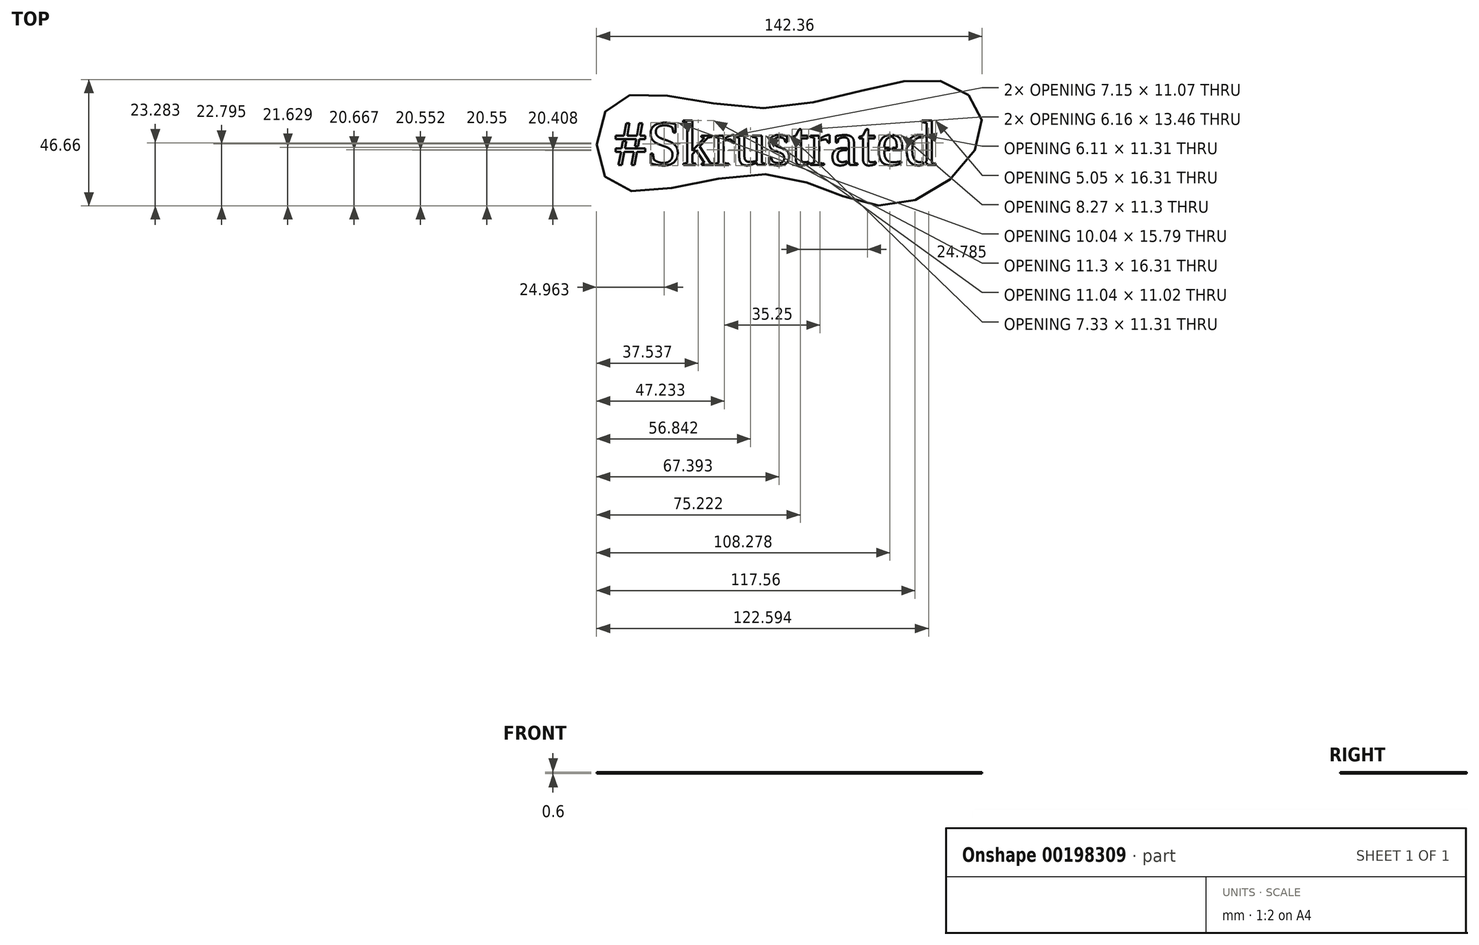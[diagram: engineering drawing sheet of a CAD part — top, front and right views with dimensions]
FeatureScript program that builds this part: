
annotation { "Feature Type Name" : "Feature", "Feature Type Description" : "" }
export const myFeature = defineFeature(function(context is Context, id is Id, definition is map)
    precondition{}
    {
        {
            var Q0;
            Q0=qCreatedBy(makeId("Top.planeOp"),FACE);
            var sketch = newSketch(context, id + "F0", { "sketchPlane" : qUnion([Q0])});
            skText(sketch, "E0", { "text": "#Skrustrated", "fontName": "Tinos-Regular.ttf"});
            skFitSpline(sketch, "E1", {"points": [v(-5.04, 14.15) * mm, v(60, 24.2) * mm, v(75.58, 5.55) * mm, v(43.18, -21.81) * mm, v(-3.93, -10.36) * mm, v(-61.05, -13.8) * mm, v(-60.94, 15.75) * mm, v(-5.04, 14.15) * mm]});
            const initialGuessF0  = {"E0": [-0.06, -0.00685, 1, 0, 0.01692]};
            skSetInitialGuess(sketch, initialGuessF0);
            skSolve(sketch);
        }
        {
            var Q0;
            Q0 = qSketchRegion(id + "F0", true);
            var Q1;
            Q1=makeQuery(id+"F0.imprint","IMPRINT",FACE,{"disambiguationData":[TD([[makeQuery(id+"F0.imprint","IMPRINT",EDGE,{"derivedFrom":sQuery(id+"F0.wireOp",EDGE,"E0.sketch_text.stroke-28")}),1.0]])]});
            var Q2;
            Q2=makeQuery(id+"F0.imprint","IMPRINT",FACE,{"disambiguationData":[TD([[makeQuery(id+"F0.imprint","IMPRINT",EDGE,{"derivedFrom":sQuery(id+"F0.wireOp",EDGE,"E0.sketch_text.stroke-220")}),1.0]])]});
            var Q3;
            Q3=makeQuery(id+"F0.imprint","IMPRINT",FACE,{"disambiguationData":[TD([[makeQuery(id+"F0.imprint","IMPRINT",EDGE,{"derivedFrom":sQuery(id+"F0.wireOp",EDGE,"E0.sketch_text.stroke-262")}),1.0]])]});
            var Q4;
            Q4=makeQuery(id+"F0.imprint","IMPRINT",FACE,{"disambiguationData":[TD([[makeQuery(id+"F0.imprint","IMPRINT",EDGE,{"derivedFrom":sQuery(id+"F0.wireOp",EDGE,"E0.sketch_text.stroke-282")}),1.0]])]});
            extrude(context, id + "F1", {"entities" : qUnion([Q0, Q1, Q2, Q3, Q4]), "depth" : 0.6 * mm});
        }
        {
            var Q0;
            Q0=makeQuery(id+"F1.opExtrude","CAP_FACE",FACE,{"disambiguationData":[OSD([sQuery(id+"F0.wireOp",EDGE,"E0.sketch_text.stroke-0"),sQuery(id+"F0.wireOp",EDGE,"E0.sketch_text.stroke-1"),sQuery(id+"F0.wireOp",EDGE,"E0.sketch_text.stroke-2"),sQuery(id+"F0.wireOp",EDGE,"E0.sketch_text.stroke-3"),sQuery(id+"F0.wireOp",EDGE,"E0.sketch_text.stroke-4"),sQuery(id+"F0.wireOp",EDGE,"E0.sketch_text.stroke-5"),sQuery(id+"F0.wireOp",EDGE,"E0.sketch_text.stroke-6"),sQuery(id+"F0.wireOp",EDGE,"E0.sketch_text.stroke-7"),sQuery(id+"F0.wireOp",EDGE,"E0.sketch_text.stroke-8"),sQuery(id+"F0.wireOp",EDGE,"E0.sketch_text.stroke-9"),sQuery(id+"F0.wireOp",EDGE,"E0.sketch_text.stroke-10"),sQuery(id+"F0.wireOp",EDGE,"E0.sketch_text.stroke-11"),sQuery(id+"F0.wireOp",EDGE,"E0.sketch_text.stroke-12"),sQuery(id+"F0.wireOp",EDGE,"E0.sketch_text.stroke-13"),sQuery(id+"F0.wireOp",EDGE,"E0.sketch_text.stroke-14"),sQuery(id+"F0.wireOp",EDGE,"E0.sketch_text.stroke-15"),sQuery(id+"F0.wireOp",EDGE,"E0.sketch_text.stroke-16"),sQuery(id+"F0.wireOp",EDGE,"E0.sketch_text.stroke-17"),sQuery(id+"F0.wireOp",EDGE,"E0.sketch_text.stroke-18"),sQuery(id+"F0.wireOp",EDGE,"E0.sketch_text.stroke-19"),sQuery(id+"F0.wireOp",EDGE,"E0.sketch_text.stroke-20"),sQuery(id+"F0.wireOp",EDGE,"E0.sketch_text.stroke-21"),sQuery(id+"F0.wireOp",EDGE,"E0.sketch_text.stroke-22"),sQuery(id+"F0.wireOp",EDGE,"E0.sketch_text.stroke-23"),sQuery(id+"F0.wireOp",EDGE,"E0.sketch_text.stroke-24"),sQuery(id+"F0.wireOp",EDGE,"E0.sketch_text.stroke-25"),sQuery(id+"F0.wireOp",EDGE,"E0.sketch_text.stroke-26"),sQuery(id+"F0.wireOp",EDGE,"E0.sketch_text.stroke-27"),sQuery(id+"F0.wireOp",EDGE,"E0.sketch_text.stroke-32"),sQuery(id+"F0.wireOp",EDGE,"E0.sketch_text.stroke-33"),sQuery(id+"F0.wireOp",EDGE,"E0.sketch_text.stroke-34"),sQuery(id+"F0.wireOp",EDGE,"E0.sketch_text.stroke-35"),sQuery(id+"F0.wireOp",EDGE,"E0.sketch_text.stroke-36"),sQuery(id+"F0.wireOp",EDGE,"E0.sketch_text.stroke-37"),sQuery(id+"F0.wireOp",EDGE,"E0.sketch_text.stroke-38"),sQuery(id+"F0.wireOp",EDGE,"E0.sketch_text.stroke-39"),sQuery(id+"F0.wireOp",EDGE,"E0.sketch_text.stroke-40"),sQuery(id+"F0.wireOp",EDGE,"E0.sketch_text.stroke-41"),sQuery(id+"F0.wireOp",EDGE,"E0.sketch_text.stroke-42"),sQuery(id+"F0.wireOp",EDGE,"E0.sketch_text.stroke-43"),sQuery(id+"F0.wireOp",EDGE,"E0.sketch_text.stroke-44"),sQuery(id+"F0.wireOp",EDGE,"E0.sketch_text.stroke-45"),sQuery(id+"F0.wireOp",EDGE,"E0.sketch_text.stroke-46"),sQuery(id+"F0.wireOp",EDGE,"E0.sketch_text.stroke-47"),sQuery(id+"F0.wireOp",EDGE,"E0.sketch_text.stroke-48"),sQuery(id+"F0.wireOp",EDGE,"E0.sketch_text.stroke-49"),sQuery(id+"F0.wireOp",EDGE,"E0.sketch_text.stroke-50"),sQuery(id+"F0.wireOp",EDGE,"E0.sketch_text.stroke-51"),sQuery(id+"F0.wireOp",EDGE,"E0.sketch_text.stroke-52"),sQuery(id+"F0.wireOp",EDGE,"E0.sketch_text.stroke-53"),sQuery(id+"F0.wireOp",EDGE,"E0.sketch_text.stroke-54"),sQuery(id+"F0.wireOp",EDGE,"E0.sketch_text.stroke-55"),sQuery(id+"F0.wireOp",EDGE,"E0.sketch_text.stroke-56"),sQuery(id+"F0.wireOp",EDGE,"E0.sketch_text.stroke-57"),sQuery(id+"F0.wireOp",EDGE,"E0.sketch_text.stroke-58"),sQuery(id+"F0.wireOp",EDGE,"E0.sketch_text.stroke-59"),sQuery(id+"F0.wireOp",EDGE,"E0.sketch_text.stroke-60"),sQuery(id+"F0.wireOp",EDGE,"E0.sketch_text.stroke-61"),sQuery(id+"F0.wireOp",EDGE,"E0.sketch_text.stroke-62"),sQuery(id+"F0.wireOp",EDGE,"E0.sketch_text.stroke-63"),sQuery(id+"F0.wireOp",EDGE,"E0.sketch_text.stroke-64"),sQuery(id+"F0.wireOp",EDGE,"E0.sketch_text.stroke-65"),sQuery(id+"F0.wireOp",EDGE,"E0.sketch_text.stroke-66"),sQuery(id+"F0.wireOp",EDGE,"E0.sketch_text.stroke-67"),sQuery(id+"F0.wireOp",EDGE,"E0.sketch_text.stroke-68"),sQuery(id+"F0.wireOp",EDGE,"E0.sketch_text.stroke-69"),sQuery(id+"F0.wireOp",EDGE,"E0.sketch_text.stroke-70"),sQuery(id+"F0.wireOp",EDGE,"E0.sketch_text.stroke-71"),sQuery(id+"F0.wireOp",EDGE,"E0.sketch_text.stroke-72"),sQuery(id+"F0.wireOp",EDGE,"E0.sketch_text.stroke-73"),sQuery(id+"F0.wireOp",EDGE,"E0.sketch_text.stroke-74"),sQuery(id+"F0.wireOp",EDGE,"E0.sketch_text.stroke-75"),sQuery(id+"F0.wireOp",EDGE,"E0.sketch_text.stroke-76"),sQuery(id+"F0.wireOp",EDGE,"E0.sketch_text.stroke-77"),sQuery(id+"F0.wireOp",EDGE,"E0.sketch_text.stroke-78"),sQuery(id+"F0.wireOp",EDGE,"E0.sketch_text.stroke-79"),sQuery(id+"F0.wireOp",EDGE,"E0.sketch_text.stroke-80"),sQuery(id+"F0.wireOp",EDGE,"E0.sketch_text.stroke-81"),sQuery(id+"F0.wireOp",EDGE,"E0.sketch_text.stroke-82"),sQuery(id+"F0.wireOp",EDGE,"E0.sketch_text.stroke-83"),sQuery(id+"F0.wireOp",EDGE,"E0.sketch_text.stroke-84"),sQuery(id+"F0.wireOp",EDGE,"E0.sketch_text.stroke-85"),sQuery(id+"F0.wireOp",EDGE,"E0.sketch_text.stroke-86"),sQuery(id+"F0.wireOp",EDGE,"E0.sketch_text.stroke-87"),sQuery(id+"F0.wireOp",EDGE,"E0.sketch_text.stroke-88"),sQuery(id+"F0.wireOp",EDGE,"E0.sketch_text.stroke-89"),sQuery(id+"F0.wireOp",EDGE,"E0.sketch_text.stroke-90"),sQuery(id+"F0.wireOp",EDGE,"E0.sketch_text.stroke-91"),sQuery(id+"F0.wireOp",EDGE,"E0.sketch_text.stroke-92"),sQuery(id+"F0.wireOp",EDGE,"E0.sketch_text.stroke-93"),sQuery(id+"F0.wireOp",EDGE,"E0.sketch_text.stroke-94"),sQuery(id+"F0.wireOp",EDGE,"E0.sketch_text.stroke-95"),sQuery(id+"F0.wireOp",EDGE,"E0.sketch_text.stroke-96"),sQuery(id+"F0.wireOp",EDGE,"E0.sketch_text.stroke-97"),sQuery(id+"F0.wireOp",EDGE,"E0.sketch_text.stroke-98"),sQuery(id+"F0.wireOp",EDGE,"E0.sketch_text.stroke-99"),sQuery(id+"F0.wireOp",EDGE,"E0.sketch_text.stroke-100"),sQuery(id+"F0.wireOp",EDGE,"E0.sketch_text.stroke-101"),sQuery(id+"F0.wireOp",EDGE,"E0.sketch_text.stroke-102"),sQuery(id+"F0.wireOp",EDGE,"E0.sketch_text.stroke-103"),sQuery(id+"F0.wireOp",EDGE,"E0.sketch_text.stroke-104"),sQuery(id+"F0.wireOp",EDGE,"E0.sketch_text.stroke-105"),sQuery(id+"F0.wireOp",EDGE,"E0.sketch_text.stroke-106"),sQuery(id+"F0.wireOp",EDGE,"E0.sketch_text.stroke-107"),sQuery(id+"F0.wireOp",EDGE,"E0.sketch_text.stroke-108"),sQuery(id+"F0.wireOp",EDGE,"E0.sketch_text.stroke-109"),sQuery(id+"F0.wireOp",EDGE,"E0.sketch_text.stroke-110"),sQuery(id+"F0.wireOp",EDGE,"E0.sketch_text.stroke-111"),sQuery(id+"F0.wireOp",EDGE,"E0.sketch_text.stroke-112"),sQuery(id+"F0.wireOp",EDGE,"E0.sketch_text.stroke-113"),sQuery(id+"F0.wireOp",EDGE,"E0.sketch_text.stroke-114"),sQuery(id+"F0.wireOp",EDGE,"E0.sketch_text.stroke-115"),sQuery(id+"F0.wireOp",EDGE,"E0.sketch_text.stroke-116"),sQuery(id+"F0.wireOp",EDGE,"E0.sketch_text.stroke-117"),sQuery(id+"F0.wireOp",EDGE,"E0.sketch_text.stroke-118"),sQuery(id+"F0.wireOp",EDGE,"E0.sketch_text.stroke-119"),sQuery(id+"F0.wireOp",EDGE,"E0.sketch_text.stroke-120"),sQuery(id+"F0.wireOp",EDGE,"E0.sketch_text.stroke-121"),sQuery(id+"F0.wireOp",EDGE,"E0.sketch_text.stroke-122"),sQuery(id+"F0.wireOp",EDGE,"E0.sketch_text.stroke-123"),sQuery(id+"F0.wireOp",EDGE,"E0.sketch_text.stroke-124"),sQuery(id+"F0.wireOp",EDGE,"E0.sketch_text.stroke-125"),sQuery(id+"F0.wireOp",EDGE,"E0.sketch_text.stroke-126"),sQuery(id+"F0.wireOp",EDGE,"E0.sketch_text.stroke-127"),sQuery(id+"F0.wireOp",EDGE,"E0.sketch_text.stroke-128"),sQuery(id+"F0.wireOp",EDGE,"E0.sketch_text.stroke-129"),sQuery(id+"F0.wireOp",EDGE,"E0.sketch_text.stroke-130"),sQuery(id+"F0.wireOp",EDGE,"E0.sketch_text.stroke-131"),sQuery(id+"F0.wireOp",EDGE,"E0.sketch_text.stroke-132"),sQuery(id+"F0.wireOp",EDGE,"E0.sketch_text.stroke-133"),sQuery(id+"F0.wireOp",EDGE,"E0.sketch_text.stroke-134"),sQuery(id+"F0.wireOp",EDGE,"E0.sketch_text.stroke-135"),sQuery(id+"F0.wireOp",EDGE,"E0.sketch_text.stroke-136"),sQuery(id+"F0.wireOp",EDGE,"E0.sketch_text.stroke-137"),sQuery(id+"F0.wireOp",EDGE,"E0.sketch_text.stroke-138"),sQuery(id+"F0.wireOp",EDGE,"E0.sketch_text.stroke-139"),sQuery(id+"F0.wireOp",EDGE,"E0.sketch_text.stroke-140"),sQuery(id+"F0.wireOp",EDGE,"E0.sketch_text.stroke-141"),sQuery(id+"F0.wireOp",EDGE,"E0.sketch_text.stroke-142"),sQuery(id+"F0.wireOp",EDGE,"E0.sketch_text.stroke-143"),sQuery(id+"F0.wireOp",EDGE,"E0.sketch_text.stroke-144"),sQuery(id+"F0.wireOp",EDGE,"E0.sketch_text.stroke-145"),sQuery(id+"F0.wireOp",EDGE,"E0.sketch_text.stroke-146"),sQuery(id+"F0.wireOp",EDGE,"E0.sketch_text.stroke-147"),sQuery(id+"F0.wireOp",EDGE,"E0.sketch_text.stroke-148"),sQuery(id+"F0.wireOp",EDGE,"E0.sketch_text.stroke-149"),sQuery(id+"F0.wireOp",EDGE,"E0.sketch_text.stroke-150"),sQuery(id+"F0.wireOp",EDGE,"E0.sketch_text.stroke-151"),sQuery(id+"F0.wireOp",EDGE,"E0.sketch_text.stroke-152"),sQuery(id+"F0.wireOp",EDGE,"E0.sketch_text.stroke-153"),sQuery(id+"F0.wireOp",EDGE,"E0.sketch_text.stroke-154"),sQuery(id+"F0.wireOp",EDGE,"E0.sketch_text.stroke-155"),sQuery(id+"F0.wireOp",EDGE,"E0.sketch_text.stroke-156"),sQuery(id+"F0.wireOp",EDGE,"E0.sketch_text.stroke-157"),sQuery(id+"F0.wireOp",EDGE,"E0.sketch_text.stroke-158"),sQuery(id+"F0.wireOp",EDGE,"E0.sketch_text.stroke-159"),sQuery(id+"F0.wireOp",EDGE,"E0.sketch_text.stroke-160"),sQuery(id+"F0.wireOp",EDGE,"E0.sketch_text.stroke-161"),sQuery(id+"F0.wireOp",EDGE,"E0.sketch_text.stroke-162"),sQuery(id+"F0.wireOp",EDGE,"E0.sketch_text.stroke-163"),sQuery(id+"F0.wireOp",EDGE,"E0.sketch_text.stroke-164"),sQuery(id+"F0.wireOp",EDGE,"E0.sketch_text.stroke-165"),sQuery(id+"F0.wireOp",EDGE,"E0.sketch_text.stroke-166"),sQuery(id+"F0.wireOp",EDGE,"E0.sketch_text.stroke-167"),sQuery(id+"F0.wireOp",EDGE,"E0.sketch_text.stroke-168"),sQuery(id+"F0.wireOp",EDGE,"E0.sketch_text.stroke-169"),sQuery(id+"F0.wireOp",EDGE,"E0.sketch_text.stroke-170"),sQuery(id+"F0.wireOp",EDGE,"E0.sketch_text.stroke-171"),sQuery(id+"F0.wireOp",EDGE,"E0.sketch_text.stroke-172"),sQuery(id+"F0.wireOp",EDGE,"E0.sketch_text.stroke-173"),sQuery(id+"F0.wireOp",EDGE,"E0.sketch_text.stroke-174"),sQuery(id+"F0.wireOp",EDGE,"E0.sketch_text.stroke-175"),sQuery(id+"F0.wireOp",EDGE,"E0.sketch_text.stroke-176"),sQuery(id+"F0.wireOp",EDGE,"E0.sketch_text.stroke-177"),sQuery(id+"F0.wireOp",EDGE,"E0.sketch_text.stroke-178"),sQuery(id+"F0.wireOp",EDGE,"E0.sketch_text.stroke-179"),sQuery(id+"F0.wireOp",EDGE,"E0.sketch_text.stroke-180"),sQuery(id+"F0.wireOp",EDGE,"E0.sketch_text.stroke-181"),sQuery(id+"F0.wireOp",EDGE,"E0.sketch_text.stroke-182"),sQuery(id+"F0.wireOp",EDGE,"E0.sketch_text.stroke-183"),sQuery(id+"F0.wireOp",EDGE,"E0.sketch_text.stroke-184"),sQuery(id+"F0.wireOp",EDGE,"E0.sketch_text.stroke-185"),sQuery(id+"F0.wireOp",EDGE,"E0.sketch_text.stroke-186"),sQuery(id+"F0.wireOp",EDGE,"E0.sketch_text.stroke-187"),sQuery(id+"F0.wireOp",EDGE,"E0.sketch_text.stroke-188"),sQuery(id+"F0.wireOp",EDGE,"E0.sketch_text.stroke-189"),sQuery(id+"F0.wireOp",EDGE,"E0.sketch_text.stroke-190"),sQuery(id+"F0.wireOp",EDGE,"E0.sketch_text.stroke-191"),sQuery(id+"F0.wireOp",EDGE,"E0.sketch_text.stroke-192"),sQuery(id+"F0.wireOp",EDGE,"E0.sketch_text.stroke-193"),sQuery(id+"F0.wireOp",EDGE,"E0.sketch_text.stroke-194"),sQuery(id+"F0.wireOp",EDGE,"E0.sketch_text.stroke-195"),sQuery(id+"F0.wireOp",EDGE,"E0.sketch_text.stroke-196"),sQuery(id+"F0.wireOp",EDGE,"E0.sketch_text.stroke-197"),sQuery(id+"F0.wireOp",EDGE,"E0.sketch_text.stroke-198"),sQuery(id+"F0.wireOp",EDGE,"E0.sketch_text.stroke-199"),sQuery(id+"F0.wireOp",EDGE,"E0.sketch_text.stroke-200"),sQuery(id+"F0.wireOp",EDGE,"E0.sketch_text.stroke-201"),sQuery(id+"F0.wireOp",EDGE,"E0.sketch_text.stroke-202"),sQuery(id+"F0.wireOp",EDGE,"E0.sketch_text.stroke-203"),sQuery(id+"F0.wireOp",EDGE,"E0.sketch_text.stroke-204"),sQuery(id+"F0.wireOp",EDGE,"E0.sketch_text.stroke-205"),sQuery(id+"F0.wireOp",EDGE,"E0.sketch_text.stroke-206"),sQuery(id+"F0.wireOp",EDGE,"E0.sketch_text.stroke-207"),sQuery(id+"F0.wireOp",EDGE,"E0.sketch_text.stroke-208"),sQuery(id+"F0.wireOp",EDGE,"E0.sketch_text.stroke-209"),sQuery(id+"F0.wireOp",EDGE,"E0.sketch_text.stroke-210"),sQuery(id+"F0.wireOp",EDGE,"E0.sketch_text.stroke-211"),sQuery(id+"F0.wireOp",EDGE,"E0.sketch_text.stroke-212"),sQuery(id+"F0.wireOp",EDGE,"E0.sketch_text.stroke-213"),sQuery(id+"F0.wireOp",EDGE,"E0.sketch_text.stroke-214"),sQuery(id+"F0.wireOp",EDGE,"E0.sketch_text.stroke-215"),sQuery(id+"F0.wireOp",EDGE,"E0.sketch_text.stroke-216"),sQuery(id+"F0.wireOp",EDGE,"E0.sketch_text.stroke-217"),sQuery(id+"F0.wireOp",EDGE,"E0.sketch_text.stroke-218"),sQuery(id+"F0.wireOp",EDGE,"E0.sketch_text.stroke-219"),sQuery(id+"F0.wireOp",EDGE,"E0.sketch_text.stroke-227"),sQuery(id+"F0.wireOp",EDGE,"E0.sketch_text.stroke-228"),sQuery(id+"F0.wireOp",EDGE,"E0.sketch_text.stroke-229"),sQuery(id+"F0.wireOp",EDGE,"E0.sketch_text.stroke-230"),sQuery(id+"F0.wireOp",EDGE,"E0.sketch_text.stroke-231"),sQuery(id+"F0.wireOp",EDGE,"E0.sketch_text.stroke-232"),sQuery(id+"F0.wireOp",EDGE,"E0.sketch_text.stroke-233"),sQuery(id+"F0.wireOp",EDGE,"E0.sketch_text.stroke-234"),sQuery(id+"F0.wireOp",EDGE,"E0.sketch_text.stroke-235"),sQuery(id+"F0.wireOp",EDGE,"E0.sketch_text.stroke-236"),sQuery(id+"F0.wireOp",EDGE,"E0.sketch_text.stroke-237"),sQuery(id+"F0.wireOp",EDGE,"E0.sketch_text.stroke-238"),sQuery(id+"F0.wireOp",EDGE,"E0.sketch_text.stroke-239"),sQuery(id+"F0.wireOp",EDGE,"E0.sketch_text.stroke-240"),sQuery(id+"F0.wireOp",EDGE,"E0.sketch_text.stroke-241"),sQuery(id+"F0.wireOp",EDGE,"E0.sketch_text.stroke-242"),sQuery(id+"F0.wireOp",EDGE,"E0.sketch_text.stroke-243"),sQuery(id+"F0.wireOp",EDGE,"E0.sketch_text.stroke-244"),sQuery(id+"F0.wireOp",EDGE,"E0.sketch_text.stroke-245"),sQuery(id+"F0.wireOp",EDGE,"E0.sketch_text.stroke-246"),sQuery(id+"F0.wireOp",EDGE,"E0.sketch_text.stroke-247"),sQuery(id+"F0.wireOp",EDGE,"E0.sketch_text.stroke-248"),sQuery(id+"F0.wireOp",EDGE,"E0.sketch_text.stroke-249"),sQuery(id+"F0.wireOp",EDGE,"E0.sketch_text.stroke-250"),sQuery(id+"F0.wireOp",EDGE,"E0.sketch_text.stroke-251"),sQuery(id+"F0.wireOp",EDGE,"E0.sketch_text.stroke-252"),sQuery(id+"F0.wireOp",EDGE,"E0.sketch_text.stroke-253"),sQuery(id+"F0.wireOp",EDGE,"E0.sketch_text.stroke-254"),sQuery(id+"F0.wireOp",EDGE,"E0.sketch_text.stroke-255"),sQuery(id+"F0.wireOp",EDGE,"E0.sketch_text.stroke-256"),sQuery(id+"F0.wireOp",EDGE,"E0.sketch_text.stroke-257"),sQuery(id+"F0.wireOp",EDGE,"E0.sketch_text.stroke-258"),sQuery(id+"F0.wireOp",EDGE,"E0.sketch_text.stroke-259"),sQuery(id+"F0.wireOp",EDGE,"E0.sketch_text.stroke-260"),sQuery(id+"F0.wireOp",EDGE,"E0.sketch_text.stroke-261"),sQuery(id+"F0.wireOp",EDGE,"E0.sketch_text.stroke-267"),sQuery(id+"F0.wireOp",EDGE,"E0.sketch_text.stroke-268"),sQuery(id+"F0.wireOp",EDGE,"E0.sketch_text.stroke-269"),sQuery(id+"F0.wireOp",EDGE,"E0.sketch_text.stroke-270"),sQuery(id+"F0.wireOp",EDGE,"E0.sketch_text.stroke-271"),sQuery(id+"F0.wireOp",EDGE,"E0.sketch_text.stroke-272"),sQuery(id+"F0.wireOp",EDGE,"E0.sketch_text.stroke-273"),sQuery(id+"F0.wireOp",EDGE,"E0.sketch_text.stroke-274"),sQuery(id+"F0.wireOp",EDGE,"E0.sketch_text.stroke-275"),sQuery(id+"F0.wireOp",EDGE,"E0.sketch_text.stroke-276"),sQuery(id+"F0.wireOp",EDGE,"E0.sketch_text.stroke-277"),sQuery(id+"F0.wireOp",EDGE,"E0.sketch_text.stroke-278"),sQuery(id+"F0.wireOp",EDGE,"E0.sketch_text.stroke-279"),sQuery(id+"F0.wireOp",EDGE,"E0.sketch_text.stroke-280"),sQuery(id+"F0.wireOp",EDGE,"E0.sketch_text.stroke-281"),sQuery(id+"F0.wireOp",EDGE,"E1")])],"isStart":false});
            var sketch = newSketch(context, id + "F2", { "sketchPlane" : qUnion([Q0])});
            skLineSegment(sketch, "E2.bottom", {"start": v(-57.83, 2.69) * mm, "end": v(-54.82, 2.69) * mm});
            skLineSegment(sketch, "E2.top", {"start": v(-57.83, 1.91) * mm, "end": v(-54.82, 1.91) * mm});
            skLineSegment(sketch, "E2.left", {"start": v(-57.83, 2.69) * mm, "end": v(-57.83, 1.91) * mm});
            skLineSegment(sketch, "E2.right", {"start": v(-54.82, 2.69) * mm, "end": v(-54.82, 1.91) * mm});
            skLineSegment(sketch, "E3.bottom", {"start": v(-53.27, -0.83) * mm, "end": v(-49.9, -0.83) * mm});
            skLineSegment(sketch, "E3.top", {"start": v(-53.27, 0) * mm, "end": v(-49.9, 0) * mm});
            skLineSegment(sketch, "E3.left", {"start": v(-53.27, -0.83) * mm, "end": v(-53.27, 0) * mm});
            skLineSegment(sketch, "E3.right", {"start": v(-49.9, -0.83) * mm, "end": v(-49.9, 0) * mm});
            skPoint(sketch, "E4.firstSnap0", {"position": v(25.72, -0.57) * mm});
            skLineSegment(sketch, "E4.bottom", {"start": v(25.72, -2.2) * mm, "end": v(26.53, -2.2) * mm});
            skLineSegment(sketch, "E4.top", {"start": v(25.72, 0) * mm, "end": v(26.53, 0) * mm});
            skLineSegment(sketch, "E4.left", {"start": v(25.72, -2.2) * mm, "end": v(25.72, 0) * mm});
            skLineSegment(sketch, "E4.right", {"start": v(26.53, -2.2) * mm, "end": v(26.53, 0) * mm});
            skLineSegment(sketch, "E5.bottom", {"start": v(26.53, -4.61) * mm, "end": v(25.73, -4.61) * mm});
            skLineSegment(sketch, "E5.top", {"start": v(26.53, -7.47) * mm, "end": v(25.73, -7.47) * mm});
            skLineSegment(sketch, "E5.left", {"start": v(26.53, -4.61) * mm, "end": v(26.53, -7.47) * mm});
            skLineSegment(sketch, "E5.right", {"start": v(25.73, -4.61) * mm, "end": v(25.73, -7.47) * mm});
            skLineSegment(sketch, "E6.bottom", {"start": v(41.88, 2.69) * mm, "end": v(42.67, 2.69) * mm});
            skLineSegment(sketch, "E6.top", {"start": v(41.88, 5.16) * mm, "end": v(42.67, 5.16) * mm});
            skLineSegment(sketch, "E6.left", {"start": v(41.88, 2.69) * mm, "end": v(41.88, 5.16) * mm});
            skLineSegment(sketch, "E6.right", {"start": v(42.67, 2.69) * mm, "end": v(42.67, 5.16) * mm});
            skLineSegment(sketch, "E7.bottom", {"start": v(41.65, 0) * mm, "end": v(42.64, 0) * mm});
            skLineSegment(sketch, "E7.top", {"start": v(41.65, -2.47) * mm, "end": v(42.64, -2.47) * mm});
            skLineSegment(sketch, "E7.left", {"start": v(41.65, 0) * mm, "end": v(41.65, -2.47) * mm});
            skLineSegment(sketch, "E7.right", {"start": v(42.64, 0) * mm, "end": v(42.64, -2.47) * mm});
            skLineSegment(sketch, "E8.bottom", {"start": v(54, -4.83) * mm, "end": v(55.04, -4.83) * mm});
            skLineSegment(sketch, "E8.top", {"start": v(54, -8.35) * mm, "end": v(55.04, -8.35) * mm});
            skLineSegment(sketch, "E8.left", {"start": v(54, -4.83) * mm, "end": v(54, -8.35) * mm});
            skLineSegment(sketch, "E8.right", {"start": v(55.04, -4.83) * mm, "end": v(55.04, -8.35) * mm});
            skLineSegment(sketch, "E9.bottom", {"start": v(53.93, 2.35) * mm, "end": v(55.18, 2.35) * mm});
            skLineSegment(sketch, "E9.top", {"start": v(53.93, 4.73) * mm, "end": v(55.18, 4.73) * mm});
            skLineSegment(sketch, "E9.left", {"start": v(53.93, 2.35) * mm, "end": v(53.93, 4.73) * mm});
            skLineSegment(sketch, "E9.right", {"start": v(55.18, 2.35) * mm, "end": v(55.18, 4.73) * mm});
            skSolve(sketch);
        }
        {
            var Q0;
            Q0 = qSketchRegion(id + "F2", true);
            extrude(context, id + "F3", {"entities" : qUnion([Q0]), "operationType" : NewBodyOperationType.ADD, "oppositeDirection" : true, "depth" : 0.6 * mm});
        }
    });
